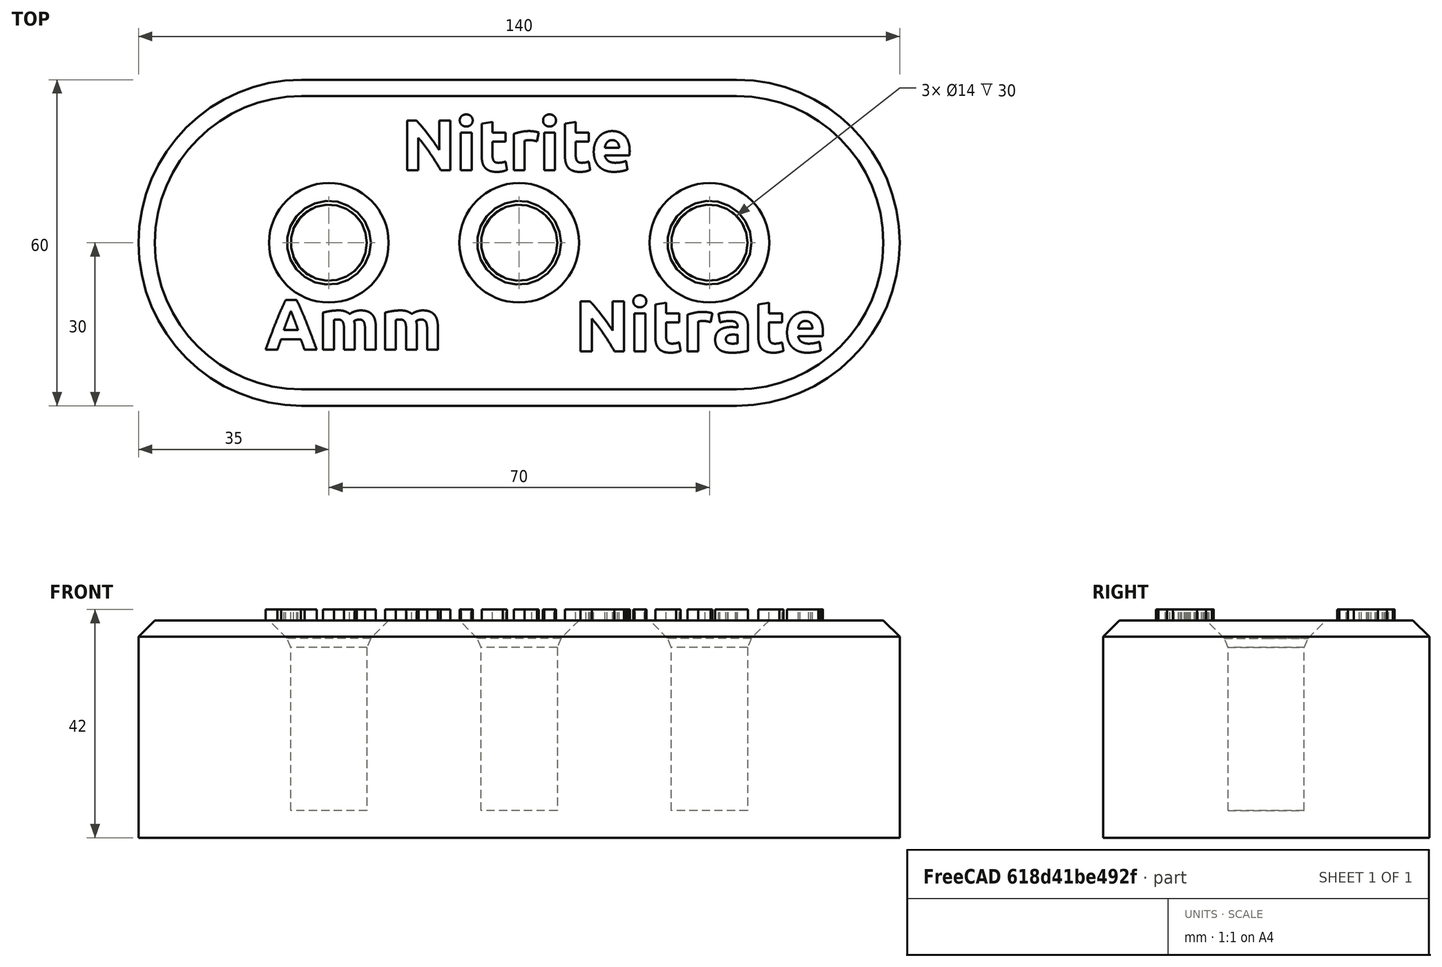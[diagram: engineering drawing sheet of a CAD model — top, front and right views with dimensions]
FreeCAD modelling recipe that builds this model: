
FCSTD DOCUMENT  (FreeCAD 0.19R)
Label: TestTubeHolder
License: All rights reserved
LicenseURL: http://en.wikipedia.org/wiki/All_rights_reserved
objects: PartDesign::Pad×4, Part::Part2DObjectPython×3, PartDesign::Chamfer×3, Sketcher::SketchObject×2, PartDesign::Pocket×1, PartDesign::Body×1, Mesh::Feature×1
note: 22 computed .brp shape members not serialized (recipe doc carries the construction recipe); baked Part::Feature solids carry a one-line shape summary decoded from their .brp

FEATURE [Sketcher::SketchObject] Sketch
  FullyConstrained = true
  MapMode = 5
  Support = -> [XY_Plane]
  sketch-geometry (4):
    g0: ArcOfCircle CenterX=-40 CenterY=0 CenterZ=0 NormalX=0 NormalY=0 NormalZ=1 AngleXU=0 Radius=30 StartAngle=1.5708 EndAngle=4.71239
    g1: ArcOfCircle CenterX=40 CenterY=0 CenterZ=0 NormalX=0 NormalY=0 NormalZ=1 AngleXU=0 Radius=30 StartAngle=4.71239 EndAngle=7.85398
    g2: LineSegment StartX=-40 StartY=-30 StartZ=0 EndX=40 EndY=-30 EndZ=0
    g3: LineSegment StartX=-40 StartY=30 StartZ=0 EndX=40 EndY=30 EndZ=0
  constraints (9):
    c: Tangent(g0,g3) = 1.5708
    c: Tangent(g0,g2) = -1.5708
    c: Tangent(g2,g1) = -1.5708
    c: Tangent(g3,g1) = 1.5708
    c: Horizontal(g2)
    c: Symmetric(g1,g0,g-2)
    c: PointOnObject(g1,g-1)
    c: Distance(g1,g1) = 60
    c: Distance(g1,g0) = 80
FEATURE [PartDesign::Pad] Pad
  Direction = (1,1,1)
  Length = 40
  Length2 = 100
  Profile = -> Sketch
  Type = 0
FEATURE [Sketcher::SketchObject] Sketch001
  FullyConstrained = true
  MapMode = 5
  Placement = pos=(0,0,40) rot=(0,0,1;0rad)
  Support = -> [Pad]
  sketch-geometry (3):
    g0: Circle CenterX=-35 CenterY=0 CenterZ=0 NormalX=0 NormalY=0 NormalZ=1 AngleXU=0 Radius=7
    g1: Circle CenterX=0 CenterY=0 CenterZ=0 NormalX=0 NormalY=0 NormalZ=1 AngleXU=0 Radius=7
    g2: Circle CenterX=35 CenterY=0 CenterZ=0 NormalX=0 NormalY=0 NormalZ=1 AngleXU=0 Radius=7
  constraints (7):
    c: PointOnObject(g0,g-1)
    c: Coincident(g1,g-1)
    c: Equal(g1,g2)
    c: Symmetric(g2,g0,g-2)
    c: Diameter(g1) = 14
    c: DistanceX(g2) = 35
    c: Equal(g0,g1)
FEATURE [PartDesign::Pocket] Pocket
  BaseFeature = -> Pad
  Length = 35
  Length2 = 100
  Profile = -> Sketch001
  Type = 0
FEATURE [Part::Part2DObjectPython] ShapeString  # Draft 2D object (typed FeaturePython)
  FontFile = <path>
  Placement = pos=(-46.76,-19.69,40) rot=(0,0,1;0rad)
  Size = 5
  String = Amm
  Tracking = 0
FEATURE [Part::Part2DObjectPython] ShapeString001  # Draft 2D object (typed FeaturePython)
  FontFile = <path>
  Placement = pos=(-21.69,13.32,40) rot=(0,0,1;0rad)
  Size = 5
  String = Nitrite
  Tracking = 0
FEATURE [Part::Part2DObjectPython] ShapeString002  # Draft 2D object (typed FeaturePython)
  FontFile = <path>
  Placement = pos=(10.24,-19.96,40) rot=(0,0,1;0rad)
  Size = 5
  String = Nitrate
  Tracking = 0
FEATURE [PartDesign::Pad] Pad001
  BaseFeature = -> Pocket
  Direction = (1,1,1)
  Length = 2
  Length2 = 100
  Profile = -> ShapeString
  Type = 0
FEATURE [PartDesign::Pad] Pad002
  BaseFeature = -> Pad001
  Direction = (1,1,1)
  Length = 2
  Length2 = 100
  Profile = -> ShapeString001
  Type = 0
FEATURE [PartDesign::Pad] Pad003
  BaseFeature = -> Pad002
  Direction = (1,1,1)
  Length = 2
  Length2 = 100
  Profile = -> ShapeString002
  Type = 0
FEATURE [PartDesign::Chamfer] Chamfer
  Angle = 45
  Base = -> Pad003 [Edge218,Edge92,Edge91]
  BaseFeature = -> Pad003
  ChamferType = 0
  FlipDirection = false
  Size = 4
  Size2 = 1
  SupportTransform = false
FEATURE [PartDesign::Chamfer] Chamfer001
  Angle = 45
  Base = -> Chamfer [Edge322,Edge958,Edge960]
  BaseFeature = -> Chamfer
  ChamferType = 0
  FlipDirection = false
  Size = 1
  Size2 = 1
  SupportTransform = false
FEATURE [PartDesign::Chamfer] Chamfer002
  Angle = 45
  Base = -> Chamfer001 [Edge6]
  BaseFeature = -> Chamfer001
  ChamferType = 0
  FlipDirection = false
  Size = 3
  Size2 = 1
  SupportTransform = false
FEATURE [PartDesign::Body] Body
  Group = -> [Sketch,Pad,Sketch001,Pocket,ShapeString,ShapeString001,ShapeString002,Pad001,Pad002,Pad003,Chamfer,Chamfer001,Chamfer002]
  Origin = -> Origin
  Tip = -> Chamfer002
FEATURE [Mesh::Feature] Mesh  label="Chamfer002 (Meshed)"
note: 3 file-system paths scrubbed to <path> (originals preserved in the JSON sidecar)
